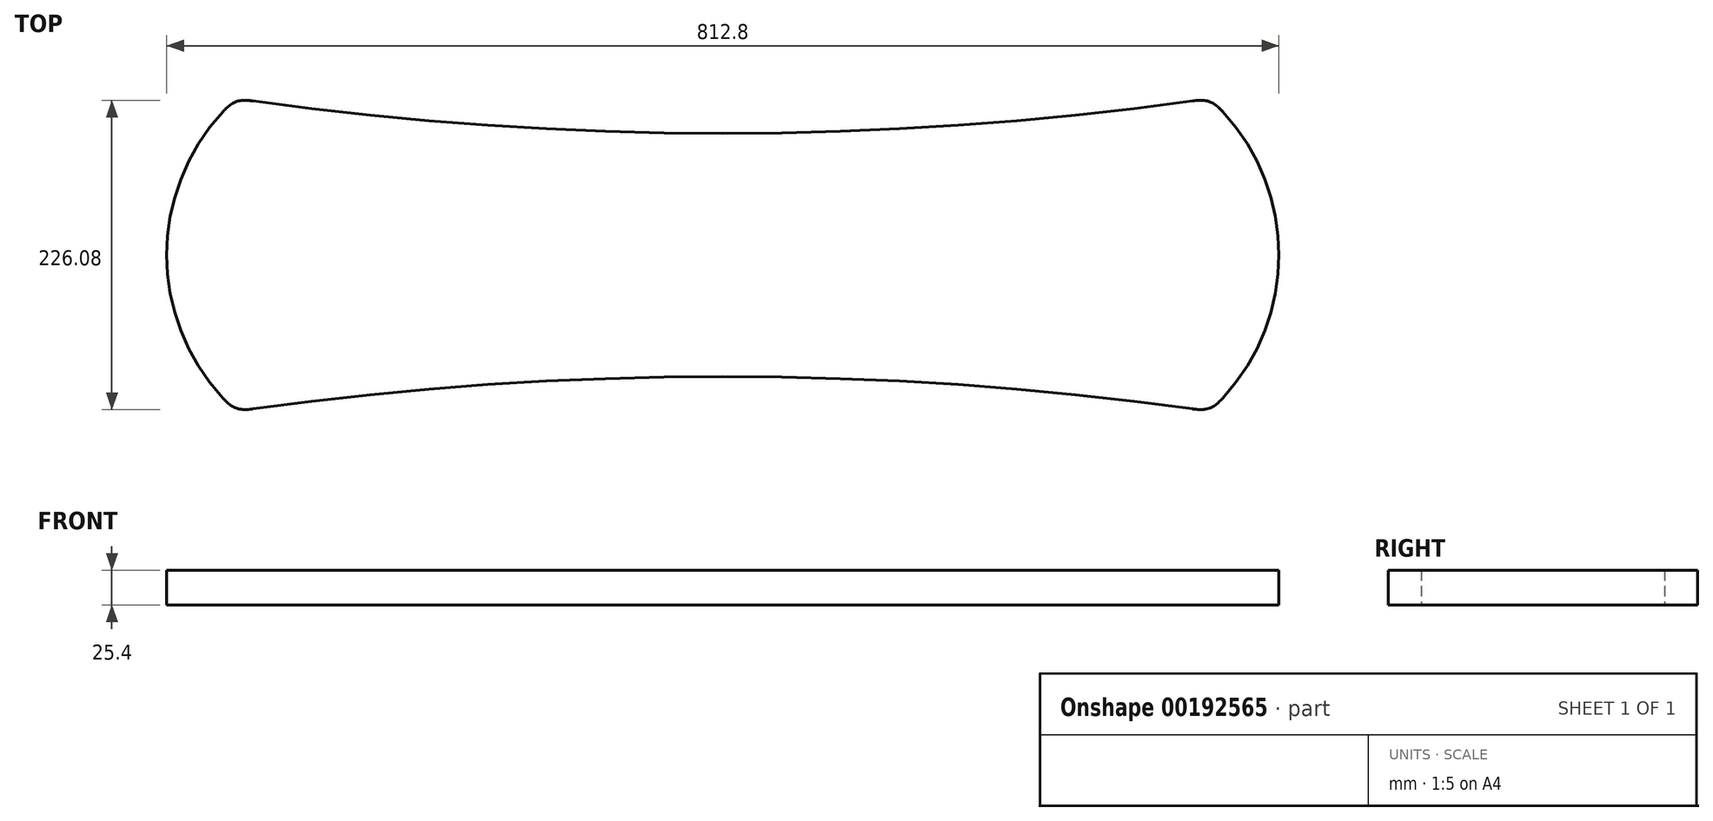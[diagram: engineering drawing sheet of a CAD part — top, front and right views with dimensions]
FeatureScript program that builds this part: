
annotation { "Feature Type Name" : "Feature", "Feature Type Description" : "" }
export const myFeature = defineFeature(function(context is Context, id is Id, definition is map)
    precondition{}
    {
        {
            var Q0;
            Q0=qCreatedBy(makeId("Top.planeOp"),FACE);
            var sketch = newSketch(context, id + "F0", { "sketchPlane" : qUnion([Q0])});
            skLineSegment(sketch, "E0.bottom", {"start": v(0, 609.6) * mm, "end": v(1219.2, 609.6) * mm});
            skLineSegment(sketch, "E0.top", {"start": v(0, 0) * mm, "end": v(1219.2, 0) * mm});
            skLineSegment(sketch, "E0.left", {"start": v(0, 609.6) * mm, "end": v(0, 0) * mm});
            skLineSegment(sketch, "E0.right", {"start": v(1219.2, 609.6) * mm, "end": v(1219.2, 0) * mm});
            skLineSegment(sketch, "E1.bottom", {"start": v(50.8, 558.8) * mm, "end": v(762, 558.8) * mm});
            skLineSegment(sketch, "E1.top", {"start": v(50.8, 330.2) * mm, "end": v(762, 330.2) * mm});
            skLineSegment(sketch, "E1.left", {"start": v(50.8, 558.8) * mm, "end": v(50.8, 330.2) * mm});
            skLineSegment(sketch, "E1.right", {"start": v(762, 558.8) * mm, "end": v(762, 330.2) * mm});
            skCircle(sketch, "E2", {"center": v(153.99, 444.5) * mm, "radius": 153.99 * mm});
            skPoint(sketch, "E2.third.point", {"position": v(0, 444.5) * mm});
            skPoint(sketch, "E2.third.point.positionSnap0", {"position": v(50.8, 444.5) * mm});
            skCircle(sketch, "E3", {"center": v(658.81, 444.5) * mm, "radius": 153.99 * mm});
            skPoint(sketch, "E3.third.point", {"position": v(812.8, 444.5) * mm});
            skPoint(sketch, "E3.third.point.positionSnap0", {"position": v(762, 444.5) * mm});
            skCircle(sketch, "E4", {"center": v(1143, 533.4) * mm, "radius": 76.2 * mm});
            skCircle(sketch, "E5", {"center": v(1143, 76.2) * mm, "radius": 76.2 * mm});
            skCircle(sketch, "E6", {"center": v(1143, 381) * mm, "radius": 76.2 * mm});
            skCircle(sketch, "E7", {"center": v(1143, 228.6) * mm, "radius": 76.2 * mm});
            skLineSegment(sketch, "E8.bottom", {"start": v(990.6, 609.6) * mm, "end": v(1066.8, 609.6) * mm});
            skLineSegment(sketch, "E8.top", {"start": v(990.6, 533.4) * mm, "end": v(1066.8, 533.4) * mm});
            skLineSegment(sketch, "E8.left", {"start": v(990.6, 609.6) * mm, "end": v(990.6, 533.4) * mm});
            skLineSegment(sketch, "E8.right", {"start": v(1066.8, 609.6) * mm, "end": v(1066.8, 533.4) * mm});
            skLineSegment(sketch, "E9.bottom", {"start": v(1066.8, 533.4) * mm, "end": v(990.6, 533.4) * mm});
            skLineSegment(sketch, "E9.top", {"start": v(1066.8, 457.2) * mm, "end": v(990.6, 457.2) * mm});
            skLineSegment(sketch, "E9.left", {"start": v(1066.8, 533.4) * mm, "end": v(1066.8, 457.2) * mm});
            skLineSegment(sketch, "E9.right", {"start": v(990.6, 533.4) * mm, "end": v(990.6, 457.2) * mm});
            skLineSegment(sketch, "E10.top", {"start": v(1066.8, 381) * mm, "end": v(990.6, 381) * mm});
            skLineSegment(sketch, "E10.left", {"start": v(1066.8, 457.2) * mm, "end": v(1066.8, 381) * mm});
            skLineSegment(sketch, "E10.right", {"start": v(990.6, 457.2) * mm, "end": v(990.6, 381) * mm});
            skLineSegment(sketch, "E11.top", {"start": v(1066.8, 304.8) * mm, "end": v(990.6, 304.8) * mm});
            skLineSegment(sketch, "E11.left", {"start": v(1066.8, 381) * mm, "end": v(1066.8, 304.8) * mm});
            skLineSegment(sketch, "E11.right", {"start": v(990.6, 381) * mm, "end": v(990.6, 304.8) * mm});
            skLineSegment(sketch, "E12.bottom", {"start": v(990.6, 304.8) * mm, "end": v(1066.8, 304.8) * mm});
            skLineSegment(sketch, "E12.top", {"start": v(990.6, 228.6) * mm, "end": v(1066.8, 228.6) * mm});
            skLineSegment(sketch, "E12.left", {"start": v(990.6, 304.8) * mm, "end": v(990.6, 228.6) * mm});
            skLineSegment(sketch, "E12.right", {"start": v(1066.8, 304.8) * mm, "end": v(1066.8, 228.6) * mm});
            skLineSegment(sketch, "E13.left", {"start": v(990.6, 228.6) * mm, "end": v(990.6, 228.6) * mm});
            skLineSegment(sketch, "E13.right", {"start": v(1066.8, 228.6) * mm, "end": v(1066.8, 228.6) * mm});
            skLineSegment(sketch, "E14.top", {"start": v(990.6, 152.4) * mm, "end": v(1066.8, 152.4) * mm});
            skLineSegment(sketch, "E14.left", {"start": v(990.6, 228.6) * mm, "end": v(990.6, 152.4) * mm});
            skLineSegment(sketch, "E14.right", {"start": v(1066.8, 228.6) * mm, "end": v(1066.8, 152.4) * mm});
            skLineSegment(sketch, "E15.bottom", {"start": v(1066.8, 152.4) * mm, "end": v(990.6, 152.4) * mm});
            skLineSegment(sketch, "E15.top", {"start": v(1066.8, 76.2) * mm, "end": v(990.6, 76.2) * mm});
            skLineSegment(sketch, "E15.left", {"start": v(1066.8, 152.4) * mm, "end": v(1066.8, 76.2) * mm});
            skLineSegment(sketch, "E15.right", {"start": v(990.6, 152.4) * mm, "end": v(990.6, 76.2) * mm});
            skLineSegment(sketch, "E16.bottom", {"start": v(990.6, 76.2) * mm, "end": v(1066.8, 76.2) * mm});
            skLineSegment(sketch, "E16.top", {"start": v(990.6, 76.2) * mm, "end": v(1066.8, 76.2) * mm});
            skLineSegment(sketch, "E16.left", {"start": v(990.6, 76.2) * mm, "end": v(990.6, 76.2) * mm});
            skLineSegment(sketch, "E16.right", {"start": v(1066.8, 76.2) * mm, "end": v(1066.8, 76.2) * mm});
            skLineSegment(sketch, "E17.top", {"start": v(990.6, 0) * mm, "end": v(1066.8, 0) * mm});
            skLineSegment(sketch, "E17.left", {"start": v(990.6, 76.2) * mm, "end": v(990.6, 0) * mm});
            skLineSegment(sketch, "E17.right", {"start": v(1066.8, 76.2) * mm, "end": v(1066.8, 0) * mm});
            skLineSegment(sketch, "E18.bottom", {"start": v(990.6, 0) * mm, "end": v(952.5, 0) * mm});
            skLineSegment(sketch, "E18.top", {"start": v(990.6, 584.2) * mm, "end": v(952.5, 584.2) * mm});
            skLineSegment(sketch, "E18.left", {"start": v(990.6, 0) * mm, "end": v(990.6, 584.2) * mm});
            skLineSegment(sketch, "E18.right", {"start": v(952.5, 0) * mm, "end": v(952.5, 584.2) * mm});
            skLineSegment(sketch, "E19.bottom", {"start": v(952.5, 0) * mm, "end": v(914.4, 0) * mm});
            skLineSegment(sketch, "E19.top", {"start": v(952.5, 177.8) * mm, "end": v(914.4, 177.8) * mm});
            skLineSegment(sketch, "E19.left", {"start": v(952.5, 0) * mm, "end": v(952.5, 177.8) * mm});
            skLineSegment(sketch, "E19.right", {"start": v(914.4, 0) * mm, "end": v(914.4, 177.8) * mm});
            skLineSegment(sketch, "E20.top", {"start": v(952.5, 355.6) * mm, "end": v(914.4, 355.6) * mm});
            skLineSegment(sketch, "E20.left", {"start": v(952.5, 177.8) * mm, "end": v(952.5, 355.6) * mm});
            skLineSegment(sketch, "E20.right", {"start": v(914.4, 177.8) * mm, "end": v(914.4, 355.6) * mm});
            skCircle(sketch, "E21", {"center": v(406.4, 3035.3) * mm, "radius": 2501.9 * mm});
            skPoint(sketch, "E21.third.point", {"position": v(406.4, 533.4) * mm});
            skPoint(sketch, "E21.third.point.positionSnap0", {"position": v(406.4, 558.8) * mm});
            skCircle(sketch, "E22", {"center": v(406.4, -2146.3) * mm, "radius": 2501.9 * mm});
            skPoint(sketch, "E22.third.point", {"position": v(406.4, 355.6) * mm});
            skPoint(sketch, "E22.third.point.positionSnap0", {"position": v(406.4, 330.2) * mm});
            skPoint(sketch, "E23", {"position": v(1028.7, 38.1) * mm});
            skPoint(sketch, "E23.positionSnap0", {"position": v(1066.8, 38.1) * mm});
            skPoint(sketch, "E23.positionSnap1", {"position": v(1028.7, 0) * mm});
            skPoint(sketch, "E24", {"position": v(1028.7, 114.3) * mm});
            skPoint(sketch, "E24.positionSnap0", {"position": v(1028.7, 76.2) * mm});
            skPoint(sketch, "E24.positionSnap1", {"position": v(990.6, 114.3) * mm});
            skPoint(sketch, "E25", {"position": v(1028.7, 190.5) * mm});
            skPoint(sketch, "E25.positionSnap0", {"position": v(990.6, 190.5) * mm});
            skPoint(sketch, "E25.positionSnap1", {"position": v(1028.7, 152.4) * mm});
            skPoint(sketch, "E26", {"position": v(1028.7, 266.7) * mm});
            skPoint(sketch, "E26.positionSnap0", {"position": v(990.6, 266.7) * mm});
            skPoint(sketch, "E27", {"position": v(1028.7, 342.9) * mm});
            skPoint(sketch, "E27.positionSnap0", {"position": v(990.6, 342.9) * mm});
            skPoint(sketch, "E28", {"position": v(1028.7, 419.1) * mm});
            skPoint(sketch, "E28.positionSnap0", {"position": v(990.6, 419.1) * mm});
            skPoint(sketch, "E29", {"position": v(1028.7, 495.3) * mm});
            skPoint(sketch, "E29.positionSnap0", {"position": v(990.6, 495.3) * mm});
            skPoint(sketch, "E30", {"position": v(1028.7, 571.5) * mm});
            skPoint(sketch, "E30.positionSnap0", {"position": v(990.6, 571.5) * mm});
            skCircle(sketch, "E31", {"center": v(1143, 533.4) * mm, "radius": 1.59 * mm});
            skCircle(sketch, "E32", {"center": v(1143, 381) * mm, "radius": 1.59 * mm});
            skCircle(sketch, "E33", {"center": v(1143, 228.6) * mm, "radius": 1.59 * mm});
            skCircle(sketch, "E34", {"center": v(1143, 76.2) * mm, "radius": 1.59 * mm});
            skCircle(sketch, "E35", {"center": v(1028.7, 571.5) * mm, "radius": 1.59 * mm});
            skCircle(sketch, "E36", {"center": v(1028.7, 495.3) * mm, "radius": 1.59 * mm});
            skCircle(sketch, "E37", {"center": v(1028.7, 419.1) * mm, "radius": 1.59 * mm});
            skCircle(sketch, "E38", {"center": v(1028.7, 342.9) * mm, "radius": 1.59 * mm});
            skCircle(sketch, "E39", {"center": v(1028.7, 266.7) * mm, "radius": 1.59 * mm});
            skCircle(sketch, "E40", {"center": v(1028.7, 190.5) * mm, "radius": 1.59 * mm});
            skCircle(sketch, "E41", {"center": v(1028.7, 114.3) * mm, "radius": 1.59 * mm});
            skCircle(sketch, "E42", {"center": v(1028.7, 38.1) * mm, "radius": 1.59 * mm});
            skSolve(sketch);
        }
        {
            var Q0;
            {var subQ0=sQuery(id+"F0.wireOp",EDGE,"E1.left");Q0=makeQuery(id+"F0.imprint","IMPRINT",FACE,{"disambiguationData":[TD([[makeQuery(id+"F0.imprint","IMPRINT",EDGE,{"derivedFrom":subQ0}),-1.0]])]});}
            var Q1;
            {var subQ1=sQuery(id+"F0.wireOp",EDGE,"E1.left");Q1=makeQuery(id+"F0.imprint","IMPRINT",FACE,{"disambiguationData":[TD([[makeQuery(id+"F0.imprint","IMPRINT",EDGE,{"derivedFrom":subQ1}),1.0]])]});}
            var Q2;
            {var subQ1=sQuery(id+"F0.wireOp",EDGE,"E1.right");Q2=makeQuery(id+"F0.imprint","IMPRINT",FACE,{"disambiguationData":[TD([[makeQuery(id+"F0.imprint","IMPRINT",EDGE,{"derivedFrom":subQ1}),-1.0]])]});}
            var Q3;
            {var subQ0=sQuery(id+"F0.wireOp",EDGE,"E1.right");Q3=makeQuery(id+"F0.imprint","IMPRINT",FACE,{"disambiguationData":[TD([[makeQuery(id+"F0.imprint","IMPRINT",EDGE,{"derivedFrom":subQ0}),1.0]])]});}
            var Q4;
            {var subQ0=sQuery(id+"F0.wireOp",EDGE,"E21");var subQ1=sQuery(id+"F0.wireOp",EDGE,"E2");var subQ2=makeQuery(id+"F0.imprint","INTERSECT",VERTEX,{"derivedFrom":[subQ1,subQ0]});Q4=makeQuery(id+"F0.imprint","IMPRINT",FACE,{"disambiguationData":[TD([[makeQuery(id+"F0.imprint","IMPRINT",EDGE,{"disambiguationData":[TD([[subQ2,1.0]])],"derivedFrom":subQ1}),-1.0]])]});}
            extrude(context, id + "F1", {"entities" : qUnion([Q0, Q1, Q2, Q3, Q4]), "depth" : 25.4 * mm});
        }
        {
            var Q0;
            Q0=makeQuery(id+"F1.opExtrude","SWEPT_EDGE",EDGE,{"disambiguationData":[OSD([sQuery(id+"F0.wireOp",EDGE,"E1.bottom"),sQuery(id+"F0.wireOp",EDGE,"E1.right"),sQuery(id+"F0.wireOp",EDGE,"E3"),sQuery(id+"F0.wireOp",EDGE,"E21")])]});
            var Q1;
            Q1=makeQuery(id+"F1.opExtrude","SWEPT_EDGE",EDGE,{"disambiguationData":[OSD([sQuery(id+"F0.wireOp",EDGE,"E1.bottom"),sQuery(id+"F0.wireOp",EDGE,"E1.left"),sQuery(id+"F0.wireOp",EDGE,"E2"),sQuery(id+"F0.wireOp",EDGE,"E21")])]});
            var Q2;
            Q2=makeQuery(id+"F1.opExtrude","SWEPT_EDGE",EDGE,{"disambiguationData":[OSD([sQuery(id+"F0.wireOp",EDGE,"E1.top"),sQuery(id+"F0.wireOp",EDGE,"E1.left"),sQuery(id+"F0.wireOp",EDGE,"E2"),sQuery(id+"F0.wireOp",EDGE,"E22")])]});
            var Q3;
            Q3=makeQuery(id+"F1.opExtrude","SWEPT_EDGE",EDGE,{"disambiguationData":[OSD([sQuery(id+"F0.wireOp",EDGE,"E1.top"),sQuery(id+"F0.wireOp",EDGE,"E1.right"),sQuery(id+"F0.wireOp",EDGE,"E3"),sQuery(id+"F0.wireOp",EDGE,"E22")])]});
            fillet(context, id + "F2", {"entities" : qUnion([Q0, Q1, Q2, Q3]), "radius" : 25.4 * mm, "rho" : 0.6, "crossSection" : FilletCrossSection.CONIC, "allowEdgeOverflow" : false});
        }
    });
